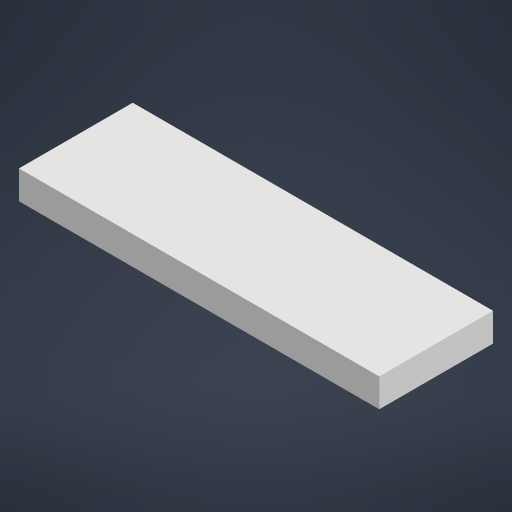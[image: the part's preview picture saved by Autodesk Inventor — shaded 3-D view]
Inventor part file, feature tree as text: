
AUTODESK INVENTOR PART (.ipt)
format: ipt  version: 2023.2 (Build 272271000, 271)  size: 150,528 bytes
history: native  units: in
note: dims shown in document units (in); Inventor stores cm internally (conversion verified against a paired STEP export)
features: extrude x1, sketch x1
ambient origin geometry x8: Origin, YZ Plane, XZ Plane, XY Plane, X Axis, Y Axis, Z Axis, Center Point
bodies: Solid1 (feature_tree)
feature tree (2):
  extrude  "Extrusion1"  Depth=12.0in
  sketch  "Sketch2"  dims[d3=38.0in d4=12.0in d5=3.0in d6=0.0in]
